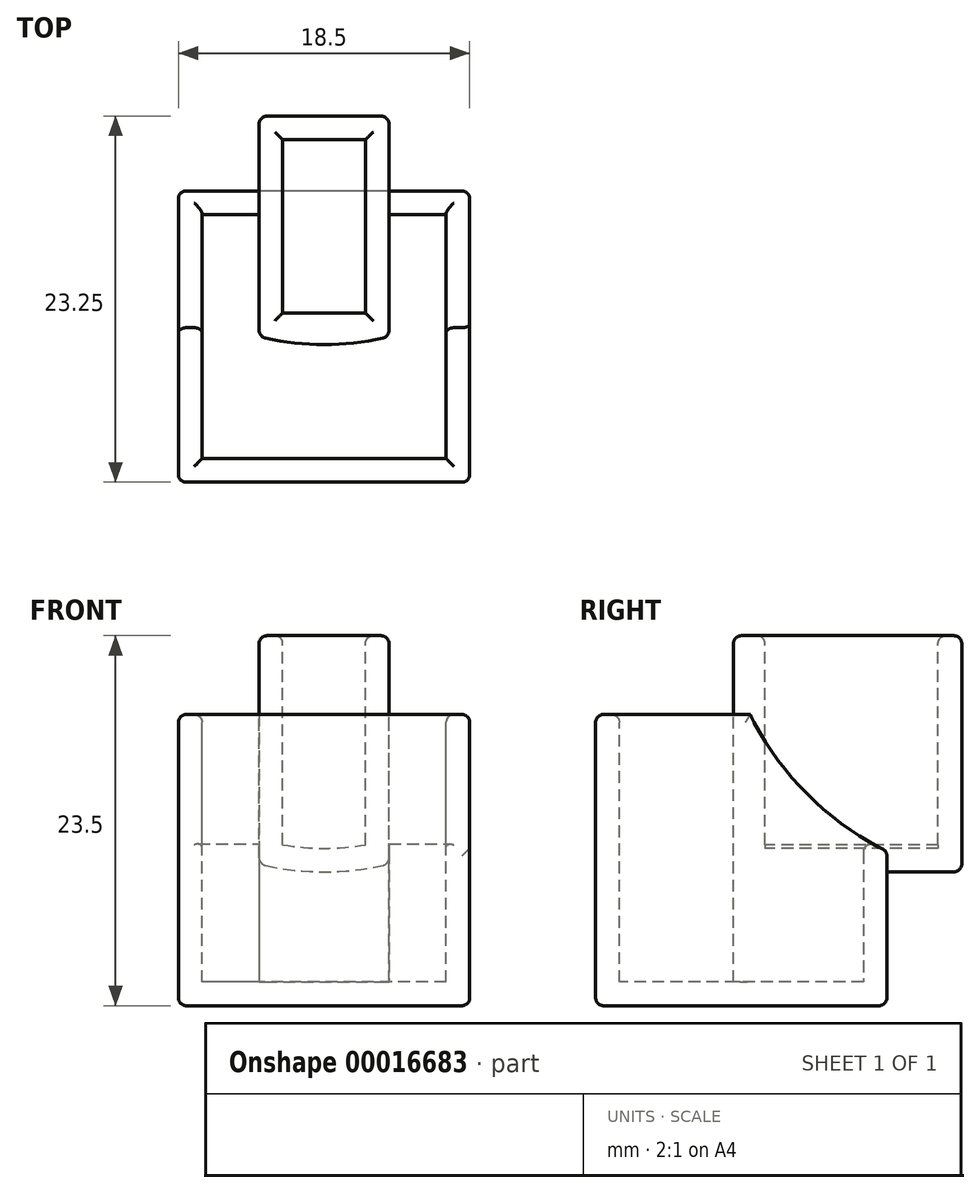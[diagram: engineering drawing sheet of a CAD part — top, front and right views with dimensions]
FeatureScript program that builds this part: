
annotation { "Feature Type Name" : "Feature", "Feature Type Description" : "" }
export const myFeature = defineFeature(function(context is Context, id is Id, definition is map)
    precondition{}
    {
        {
            var Q0;
            Q0=qCreatedBy(makeId("Top.planeOp"),FACE);
            var sketch = newSketch(context, id + "F0", { "sketchPlane" : qUnion([Q0])});
            skLineSegment(sketch, "E0.rect.bottom", {"start": v(9.25, 9.25) * mm, "end": v(-9.25, 9.25) * mm});
            skLineSegment(sketch, "E0.rect.top", {"start": v(9.25, -9.25) * mm, "end": v(-9.25, -9.25) * mm});
            skLineSegment(sketch, "E0.rect.left", {"start": v(9.25, 9.25) * mm, "end": v(9.25, -9.25) * mm});
            skLineSegment(sketch, "E0.rect.right", {"start": v(-9.25, 9.25) * mm, "end": v(-9.25, -9.25) * mm});
            skPoint(sketch, "E0.rect.middle", {"position": v(0, 0) * mm});
            skSolve(sketch);
        }
        {
            var Q0;
            Q0=makeQuery(id+"F0.imprint","IMPRINT",FACE,{"disambiguationData":[TD([[makeQuery(id+"F0.imprint","IMPRINT",EDGE,{"derivedFrom":sQuery(id+"F0.wireOp",EDGE,"E0.rect.bottom")}),1.0]])]});
            extrude(context, id + "F1", {"entities" : qUnion([Q0]), "oppositeDirection" : true, "depth" : 18.5 * mm});
        }
        {
            var Q0;
            Q0=makeQuery(id+"F1.opExtrude","SWEPT_FACE",FACE,{"disambiguationData":[OSD([sQuery(id+"F0.wireOp",EDGE,"E0.rect.left")])]});
            var sketch = newSketch(context, id + "F2", { "sketchPlane" : qUnion([Q0])});
            skPoint(sketch, "E1", {"position": v(2, 0) * mm});
            skPoint(sketch, "E2", {"position": v(-9.25, -18.5) * mm});
            skPoint(sketch, "E3", {"position": v(4.19, -5.06) * mm});
            skCircle(sketch, "E4", {"center": v(17.62, 8.37) * mm, "radius": 19 * mm});
            skSolve(sketch);
        }
        {
            var Q0;
            Q0 = qSketchRegion(id + "F2", true);
            extrude(context, id + "F3", {"entities" : qUnion([Q0]), "operationType" : NewBodyOperationType.REMOVE, "oppositeDirection" : true, "depth" : 25.4 * mm});
        }
        {
            var Q0;
            Q0=makeQuery(id+"F1.opExtrude","CAP_FACE",FACE,{"disambiguationData":[OSD([sQuery(id+"F0.wireOp",EDGE,"E0.rect.bottom"),sQuery(id+"F0.wireOp",EDGE,"E0.rect.top"),sQuery(id+"F0.wireOp",EDGE,"E0.rect.left"),sQuery(id+"F0.wireOp",EDGE,"E0.rect.right")])],"isStart":true});
            var Q1;
            Q1=makeQuery(id+"F3.boolean.opBoolean","COPY",FACE,{"derivedFrom":makeQuery(id+"F3.opExtrude","SWEPT_FACE",FACE,{"disambiguationData":[OSD([sQuery(id+"F2.wireOp",EDGE,"E4")])]})});
            shell(context, id + "F4", {"entities" : qUnion([Q0, Q1]), "thickness" : 1.5 * mm});
        }
        {
            var Q0;
            Q0=qCreatedBy(makeId("Front.planeOp"),FACE);
            var sketch = newSketch(context, id + "F5", { "sketchPlane" : qUnion([Q0])});
            skPoint(sketch, "E5", {"position": v(0, 5) * mm});
            skLineSegment(sketch, "E6", {"start": v(0, 5) * mm, "end": v(0, -9.5) * mm});
            skLineSegment(sketch, "E7.top", {"start": v(4.12, 5) * mm, "end": v(-4.12, 5) * mm});
            skLineSegment(sketch, "E7.left", {"start": v(4.12, -9.5) * mm, "end": v(4.12, 5) * mm});
            skLineSegment(sketch, "E7.right", {"start": v(-4.12, -9.5) * mm, "end": v(-4.12, 5) * mm});
            skPoint(sketch, "E8", {"position": v(0, -10) * mm});
            skArc(sketch, "E9", {"start": v(-4.12, -9.5) * mm, "mid": v(0, -10) * mm, "end": v(4.13, -9.5) * mm});
            skSolve(sketch);
        }
        {
            var Q0;
            Q0 = qSketchRegion(id + "F5", true);
            extrude(context, id + "F6", {"entities" : qUnion([Q0]), "operationType" : NewBodyOperationType.ADD, "oppositeDirection" : true, "depth" : 14 * mm});
        }
        {
            var Q0;
            Q0=makeQuery(id+"F6.opExtrude","SWEPT_FACE",FACE,{"disambiguationData":[OSD([sQuery(id+"F5.wireOp",EDGE,"E7.top")])]});
            shell(context, id + "F7", {"entities" : qUnion([Q0]), "thickness" : 1.5 * mm});
        }
        {
            var Q0;
            Q0=makeQuery(id+"F6.opExtrude","SWEPT_FACE",FACE,{"disambiguationData":[OSD([sQuery(id+"F5.wireOp",EDGE,"E7.top")])]});
            var sketch = newSketch(context, id + "F8", { "sketchPlane" : qUnion([Q0])});
            skArc(sketch, "E10", {"start": v(-4.13, 0) * mm, "mid": v(0, -0.5) * mm, "end": v(4.12, 0) * mm});
            skLineSegment(sketch, "E11", {"start": v(-4.13, 0) * mm, "end": v(4.12, 0) * mm});
            skSolve(sketch);
        }
        {
            var Q0;
            Q0=makeQuery(id+"F8.imprint","IMPRINT",FACE,{"disambiguationData":[TD([[makeQuery(id+"F8.imprint","IMPRINT",EDGE,{"derivedFrom":sQuery(id+"F8.wireOp",EDGE,"E10")}),1.0]])]});
            extrude(context, id + "F9", {"entities" : qUnion([Q0]), "operationType" : NewBodyOperationType.ADD, "oppositeDirection" : true, "depth" : 23.32 * mm});
        }
        {
            var Q0;
            Q0=makeQuery(id+"F9.opExtrude","SWEPT_FACE",FACE,{"disambiguationData":[OSD([sQuery(id+"F8.wireOp",EDGE,"E11")])]});
            extrude(context, id + "F10", {"entities" : qUnion([Q0]), "operationType" : NewBodyOperationType.ADD, "depth" : 8.55 * mm});
        }
        {
            var Q0;
            Q0=makeQuery(id+"F3.boolean.opBoolean","INTERSECT",EDGE,{"derivedFrom":[makeQuery(id+"F1.opExtrude","SWEPT_FACE",FACE,{"disambiguationData":[OSD([sQuery(id+"F0.wireOp",EDGE,"E0.rect.right")])]}),makeQuery(id+"F3.opExtrude","SWEPT_FACE",FACE,{"disambiguationData":[OSD([sQuery(id+"F2.wireOp",EDGE,"E4")])]})]});
            var Q1;
            Q1=makeQuery(id+"F1.opExtrude","CAP_EDGE",EDGE,{"disambiguationData":[OSD([sQuery(id+"F0.wireOp",EDGE,"E0.rect.right")])],"isStart":true});
            var Q2;
            Q2=makeQuery(id+"F1.opExtrude","SWEPT_EDGE",EDGE,{"disambiguationData":[OSD([sQuery(id+"F0.wireOp",EDGE,"E0.rect.top"),sQuery(id+"F0.wireOp",EDGE,"E0.rect.right")])]});
            var Q3;
            Q3=makeQuery(id+"F1.opExtrude","CAP_EDGE",EDGE,{"disambiguationData":[OSD([sQuery(id+"F0.wireOp",EDGE,"E0.rect.right")])],"isStart":false});
            var Q4;
            Q4=makeQuery(id+"F1.opExtrude","SWEPT_EDGE",EDGE,{"disambiguationData":[OSD([sQuery(id+"F0.wireOp",EDGE,"E0.rect.bottom"),sQuery(id+"F0.wireOp",EDGE,"E0.rect.right")])]});
            var Q5;
            Q5=makeQuery(id+"F6.opExtrude","SWEPT_EDGE",EDGE,{"disambiguationData":[OSD([sQuery(id+"F5.wireOp",EDGE,"E7.top"),sQuery(id+"F5.wireOp",EDGE,"E7.right")])]});
            var Q6;
            Q6=makeQuery(id+"F6.opExtrude","CAP_EDGE",EDGE,{"disambiguationData":[OSD([sQuery(id+"F5.wireOp",EDGE,"E7.right")])],"isStart":false});
            var Q7;
            Q7=makeQuery(id+"F6.opExtrude","CAP_EDGE",EDGE,{"disambiguationData":[OSD([sQuery(id+"F5.wireOp",EDGE,"E7.top")])],"isStart":false});
            var Q8;
            {var subQ0=sQuery(id+"F5.wireOp",EDGE,"E7.right");var subQ1=sQuery(id+"F5.wireOp",EDGE,"E9");Q8=makeQuery(id+"F6.boolean.opBoolean","SPLIT",EDGE,{"disambiguationData":[TD([makeQuery(id+"F1.opExtrude","SWEPT_FACE",FACE,{"disambiguationData":[OSD([sQuery(id+"F0.wireOp",EDGE,"E0.rect.bottom")])]})])],"derivedFrom":makeQuery(id+"F6.opExtrude","SWEPT_EDGE",EDGE,{"disambiguationData":[OSD([subQ0,subQ1])]})});}
            var Q9;
            {var subQ0=sQuery(id+"F0.wireOp",EDGE,"E0.rect.bottom");var subQ1=sQuery(id+"F2.wireOp",EDGE,"E4");Q9=makeQuery(id+"F6.boolean.opBoolean","SPLIT",EDGE,{"disambiguationData":[TD([makeQuery(id+"F4.opShell","OFFSET_FACE",FACE,{"disambiguationData":[OSD([sQuery(id+"F0.wireOp",EDGE,"E0.rect.right")])]})])],"derivedFrom":makeQuery(id+"F4.opShell","OFFSET_EDGE",EDGE,{"disambiguationData":[OSD([subQ0,subQ1])]})});}
            var Q10;
            Q10=makeQuery(id+"F4.opShell","OFFSET_EDGE",EDGE,{"disambiguationData":[OSD([sQuery(id+"F0.wireOp",EDGE,"E0.rect.right"),sQuery(id+"F2.wireOp",EDGE,"E4")])]});
            var Q11;
            {var subQ0=makeQuery(id+"F1.opExtrude","SWEPT_FACE",FACE,{"disambiguationData":[OSD([sQuery(id+"F0.wireOp",EDGE,"E0.rect.bottom")])]});var subQ1=makeQuery(id+"F3.opExtrude","SWEPT_FACE",FACE,{"disambiguationData":[OSD([sQuery(id+"F2.wireOp",EDGE,"E4")])]});Q11=makeQuery(id+"F6.boolean.opBoolean","SPLIT",EDGE,{"disambiguationData":[TD([makeQuery(id+"F1.opExtrude","SWEPT_FACE",FACE,{"disambiguationData":[OSD([sQuery(id+"F0.wireOp",EDGE,"E0.rect.right")])]})])],"derivedFrom":makeQuery(id+"F3.boolean.opBoolean","INTERSECT",EDGE,{"derivedFrom":[subQ0,subQ1]})});}
            var Q12;
            {var subQ0=sQuery(id+"F0.wireOp",EDGE,"E0.rect.right");Q12=makeQuery(id+"F4.opShell","OFFSET_EDGE",EDGE,{"disambiguationData":[OSD([subQ0]),TDD([makeQuery(id+"F1.opExtrude","CAP_EDGE",EDGE,{"disambiguationData":[OSD([subQ0])],"isStart":true})])]});}
            var Q13;
            {var subQ0=sQuery(id+"F0.wireOp",EDGE,"E0.rect.top");Q13=makeQuery(id+"F4.opShell","OFFSET_EDGE",EDGE,{"disambiguationData":[OSD([subQ0]),TDD([makeQuery(id+"F1.opExtrude","CAP_EDGE",EDGE,{"disambiguationData":[OSD([subQ0])],"isStart":true})])]});}
            var Q14;
            Q14=makeQuery(id+"F1.opExtrude","CAP_EDGE",EDGE,{"disambiguationData":[OSD([sQuery(id+"F0.wireOp",EDGE,"E0.rect.top")])],"isStart":true});
            var Q15;
            Q15=makeQuery(id+"F1.opExtrude","CAP_EDGE",EDGE,{"disambiguationData":[OSD([sQuery(id+"F0.wireOp",EDGE,"E0.rect.left")])],"isStart":true});
            var Q16;
            {var subQ0=sQuery(id+"F0.wireOp",EDGE,"E0.rect.left");Q16=makeQuery(id+"F4.opShell","OFFSET_EDGE",EDGE,{"disambiguationData":[OSD([subQ0]),TDD([makeQuery(id+"F1.opExtrude","CAP_EDGE",EDGE,{"disambiguationData":[OSD([subQ0])],"isStart":true})])]});}
            var Q17;
            Q17=makeQuery(id+"F3.boolean.opBoolean","COPY",EDGE,{"derivedFrom":makeQuery(id+"F3.opExtrude","CAP_EDGE",EDGE,{"disambiguationData":[OSD([sQuery(id+"F2.wireOp",EDGE,"E4")])],"isStart":true})});
            var Q18;
            Q18=makeQuery(id+"F4.opShell","OFFSET_EDGE",EDGE,{"disambiguationData":[OSD([sQuery(id+"F2.wireOp",EDGE,"E4")])]});
            var Q19;
            {var subQ0=sQuery(id+"F0.wireOp",EDGE,"E0.rect.bottom");var subQ1=sQuery(id+"F2.wireOp",EDGE,"E4");Q19=makeQuery(id+"F6.boolean.opBoolean","SPLIT",EDGE,{"disambiguationData":[TD([makeQuery(id+"F4.opShell","OFFSET_FACE",FACE,{"disambiguationData":[OSD([sQuery(id+"F0.wireOp",EDGE,"E0.rect.left")])]})])],"derivedFrom":makeQuery(id+"F4.opShell","OFFSET_EDGE",EDGE,{"disambiguationData":[OSD([subQ0,subQ1])]})});}
            var Q20;
            {var subQ0=makeQuery(id+"F1.opExtrude","SWEPT_FACE",FACE,{"disambiguationData":[OSD([sQuery(id+"F0.wireOp",EDGE,"E0.rect.bottom")])]});var subQ1=makeQuery(id+"F3.opExtrude","SWEPT_FACE",FACE,{"disambiguationData":[OSD([sQuery(id+"F2.wireOp",EDGE,"E4")])]});Q20=makeQuery(id+"F6.boolean.opBoolean","SPLIT",EDGE,{"disambiguationData":[TD([makeQuery(id+"F1.opExtrude","SWEPT_FACE",FACE,{"disambiguationData":[OSD([sQuery(id+"F0.wireOp",EDGE,"E0.rect.left")])]})])],"derivedFrom":makeQuery(id+"F3.boolean.opBoolean","INTERSECT",EDGE,{"derivedFrom":[subQ0,subQ1]})});}
            var Q21;
            Q21=makeQuery(id+"F1.opExtrude","CAP_EDGE",EDGE,{"disambiguationData":[OSD([sQuery(id+"F0.wireOp",EDGE,"E0.rect.bottom")])],"isStart":false});
            var Q22;
            Q22=makeQuery(id+"F1.opExtrude","SWEPT_EDGE",EDGE,{"disambiguationData":[OSD([sQuery(id+"F0.wireOp",EDGE,"E0.rect.bottom"),sQuery(id+"F0.wireOp",EDGE,"E0.rect.left")])]});
            var Q23;
            Q23=makeQuery(id+"F1.opExtrude","CAP_EDGE",EDGE,{"disambiguationData":[OSD([sQuery(id+"F0.wireOp",EDGE,"E0.rect.left")])],"isStart":false});
            var Q24;
            Q24=makeQuery(id+"F1.opExtrude","SWEPT_EDGE",EDGE,{"disambiguationData":[OSD([sQuery(id+"F0.wireOp",EDGE,"E0.rect.top"),sQuery(id+"F0.wireOp",EDGE,"E0.rect.left")])]});
            var Q25;
            Q25=makeQuery(id+"F6.opExtrude","SWEPT_EDGE",EDGE,{"disambiguationData":[OSD([sQuery(id+"F5.wireOp",EDGE,"E7.top"),sQuery(id+"F5.wireOp",EDGE,"E7.left")])]});
            var Q26;
            Q26=makeQuery(id+"F6.opExtrude","CAP_EDGE",EDGE,{"disambiguationData":[OSD([sQuery(id+"F5.wireOp",EDGE,"E7.left")])],"isStart":false});
            var Q27;
            Q27=makeQuery(id+"F1.opExtrude","CAP_EDGE",EDGE,{"disambiguationData":[OSD([sQuery(id+"F0.wireOp",EDGE,"E0.rect.top")])],"isStart":false});
            var Q28;
            Q28=makeQuery(id+"F9.opExtrude","CAP_EDGE",EDGE,{"disambiguationData":[OSD([sQuery(id+"F8.wireOp",EDGE,"E10")])],"isStart":true});
            var Q29;
            Q29=makeQuery(id+"F7.opShell","OFFSET_EDGE",EDGE,{"disambiguationData":[OSD([sQuery(id+"F5.wireOp",EDGE,"E7.top"),sQuery(id+"F5.wireOp",EDGE,"E7.right")])]});
            var Q30;
            {var subQ0=sQuery(id+"F5.wireOp",EDGE,"E7.top");Q30=makeQuery(id+"F7.opShell","OFFSET_EDGE",EDGE,{"disambiguationData":[OSD([subQ0]),TDD([makeQuery(id+"F6.opExtrude","CAP_EDGE",EDGE,{"disambiguationData":[OSD([subQ0])],"isStart":false})])]});}
            var Q31;
            Q31=makeQuery(id+"F7.opShell","OFFSET_EDGE",EDGE,{"disambiguationData":[OSD([sQuery(id+"F5.wireOp",EDGE,"E7.top"),sQuery(id+"F5.wireOp",EDGE,"E7.left")])]});
            var Q32;
            {var subQ0=sQuery(id+"F5.wireOp",EDGE,"E7.top");Q32=makeQuery(id+"F7.opShell","OFFSET_EDGE",EDGE,{"disambiguationData":[OSD([subQ0]),TDD([makeQuery(id+"F6.opExtrude","CAP_EDGE",EDGE,{"disambiguationData":[OSD([subQ0])],"isStart":true})])]});}
            var Q33;
            {var subQ0=sQuery(id+"F5.wireOp",EDGE,"E7.left");var subQ1=sQuery(id+"F5.wireOp",EDGE,"E9");Q33=makeQuery(id+"F6.boolean.opBoolean","SPLIT",EDGE,{"disambiguationData":[TD([makeQuery(id+"F1.opExtrude","SWEPT_FACE",FACE,{"disambiguationData":[OSD([sQuery(id+"F0.wireOp",EDGE,"E0.rect.bottom")])]})])],"derivedFrom":makeQuery(id+"F6.opExtrude","SWEPT_EDGE",EDGE,{"disambiguationData":[OSD([subQ0,subQ1])]})});}
            var Q34;
            Q34=makeQuery(id+"F6.opExtrude","CAP_EDGE",EDGE,{"disambiguationData":[OSD([sQuery(id+"F5.wireOp",EDGE,"E9")])],"isStart":false});
            var Q35;
            {var subQ0=sQuery(id+"F5.wireOp",EDGE,"E7.right");var subQ1=sQuery(id+"F5.wireOp",EDGE,"E7.top");var subQ2=sQuery(id+"F8.wireOp",EDGE,"E10");var subQ3=sQuery(id+"F8.wireOp",EDGE,"E11");var subQ4=makeQuery(id+"F9.opExtrude","SWEPT_EDGE",EDGE,{"disambiguationData":[OSD([subQ1,subQ0,subQ2,subQ3])]});Q35=makeQuery(id+"F10.boolean.opBoolean","MERGE",EDGE,{"derivedFrom":[makeQuery(id+"F9.boolean.opBoolean","MERGE",EDGE,{"derivedFrom":[makeQuery(id+"F6.opExtrude","CAP_EDGE",EDGE,{"disambiguationData":[OSD([subQ0])],"isStart":true}),subQ4]}),subQ4,makeQuery(id+"F10.opExtrude","CAP_EDGE",EDGE,{"disambiguationData":[OSD([subQ1,subQ0,subQ2,subQ3])],"isStart":true})]});}
            var Q36;
            {var subQ0=sQuery(id+"F5.wireOp",EDGE,"E7.left");var subQ1=sQuery(id+"F5.wireOp",EDGE,"E7.top");var subQ2=sQuery(id+"F8.wireOp",EDGE,"E10");var subQ3=sQuery(id+"F8.wireOp",EDGE,"E11");var subQ4=makeQuery(id+"F9.opExtrude","SWEPT_EDGE",EDGE,{"disambiguationData":[OSD([subQ1,subQ0,subQ2,subQ3])]});Q36=makeQuery(id+"F10.boolean.opBoolean","MERGE",EDGE,{"derivedFrom":[makeQuery(id+"F9.boolean.opBoolean","MERGE",EDGE,{"derivedFrom":[makeQuery(id+"F6.opExtrude","CAP_EDGE",EDGE,{"disambiguationData":[OSD([subQ0])],"isStart":true}),subQ4]}),subQ4,makeQuery(id+"F10.opExtrude","CAP_EDGE",EDGE,{"disambiguationData":[OSD([subQ1,subQ0,subQ2,subQ3])],"isStart":true})]});}
            fillet(context, id + "F11", {"entities" : qUnion([Q0, Q1, Q2, Q3, Q4, Q5, Q6, Q7, Q8, Q9, Q10, Q11, Q12, Q13, Q14, Q15, Q16, Q17, Q18, Q19, Q20, Q21, Q22, Q23, Q24, Q25, Q26, Q27, Q28, Q29, Q30, Q31, Q32, Q33, Q34, Q35, Q36]), "radius" : .5 * mm, "tangentPropagation" : true, "allowEdgeOverflow" : false});
        }
    });
